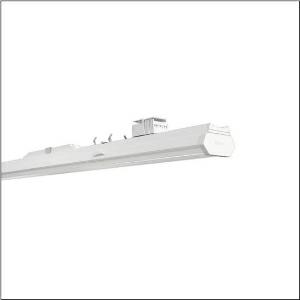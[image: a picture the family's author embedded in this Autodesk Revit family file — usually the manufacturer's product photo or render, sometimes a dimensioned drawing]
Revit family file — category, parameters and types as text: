
# Revit family: licross_r__11_protected_mo_51ts12dn48xf3s4_12c4
name_source: partatom
category: Lighting Fixtures
units: mm (PartAtom-declared; Revit-internal decimal feet)

## family parameters
Cut with Voids When Loaded = No
Host = Face
Light Source = No
Part Type = Normal
Room Calculation Point = No
Round Connector Dimension = Use Diameter
Shared = No

## types (1)
- --- (1 x LED, 8470 lm, 60 W, 4000K)
    Apparent Load = 60 VA
    CIE Flux Codes = 54 82 95 97 100
    Color Rendering = 80
    Color Temperature = 4000K
    Default Elevation = 1800 mm
    Description = Licross® 11 Protected MO, luminaire insert, of sheet steel, galvanised, coil coated, white, length: 1.500mm, width: 90mm, height: 101mm, LED rated luminous flux: 8.470lm, light colour: 840, control gear: DALI 2, control gear: ECG DALI, with plug, 6-pole, with phase selection, for trunking rail, 9 or 11-core, mains connection: 220..240V, AC/DC, 0/50..60Hz, halogen-free wiring, for emergency light function, converter,control gear: single battery element, battery: LiFeP04, 9Ah, primary optical cover: cover, of PMMA, light emission: direct with ceiling illumination distribution, primary light characteristic: symmetric, protection rating (complete): IP50, insulation class (complete): insulation class I (protective earthing), certification: CE, UKCA, protection symbol: D if used in an environment with non-conductive dust loads with corresponding accessories, permissible ambient temperature for indoor applications: +5..+35°C, standard: EN 60598-2-22, corresponds to IFS (International Featured Standards) requirements for safety and quality in the food industry, reducing of maximum allowable ambient temperature of 5°C with ceiling mounting, LABS conformity tested according to VDMA 24364:2018-05, packaging unit: 1 piece
    Height = 92 mm
    Lamp = 1 x LED
    Lamp Light Flux = 8470 lm
    Lamp Power = 60 W
    Lamp count = 1
    Length = 1500 mm
    Luminous efficacy = 141 lm/W
    Manufacturer = Siteco
    ModVariant = No
    Model = 51TS12DN48XF3S4
    Mounting Place = Ceiling
    Mounting Type = Pendant
    Number of Poles = 1
    OnlyDefault = Yes
    Power Factor = 1
    Product Name = Licross® 11 Protected MO
    Product group = luminaire insert
    ProductGroupID = 902
    Protection Class = Protection class I
    Protection Degree = IP 50
    RLX_Detail_Level = 1
    RlxData = <blob elided: 24681 chars, md5=5b7010de>
    Socket = socket
    Standby Power = 0 W
    System Light Flux = 8470 lm
    System Power = 60 W
    Type Comments = : AC-mode, luminous flux: 100 % | dim-lin: 254 | 370 mA
    Type Image = l_1256145.jpg
    URL = http://relux.com
    VarID = @adj_115739
    Voltage = 0 V
    Weight = 0.00 kg
    Width = 88 mm

## geometry (parser evidence)
native form markers: Blend x4, Sweep x11
no freeform markers — native parametric forms only
